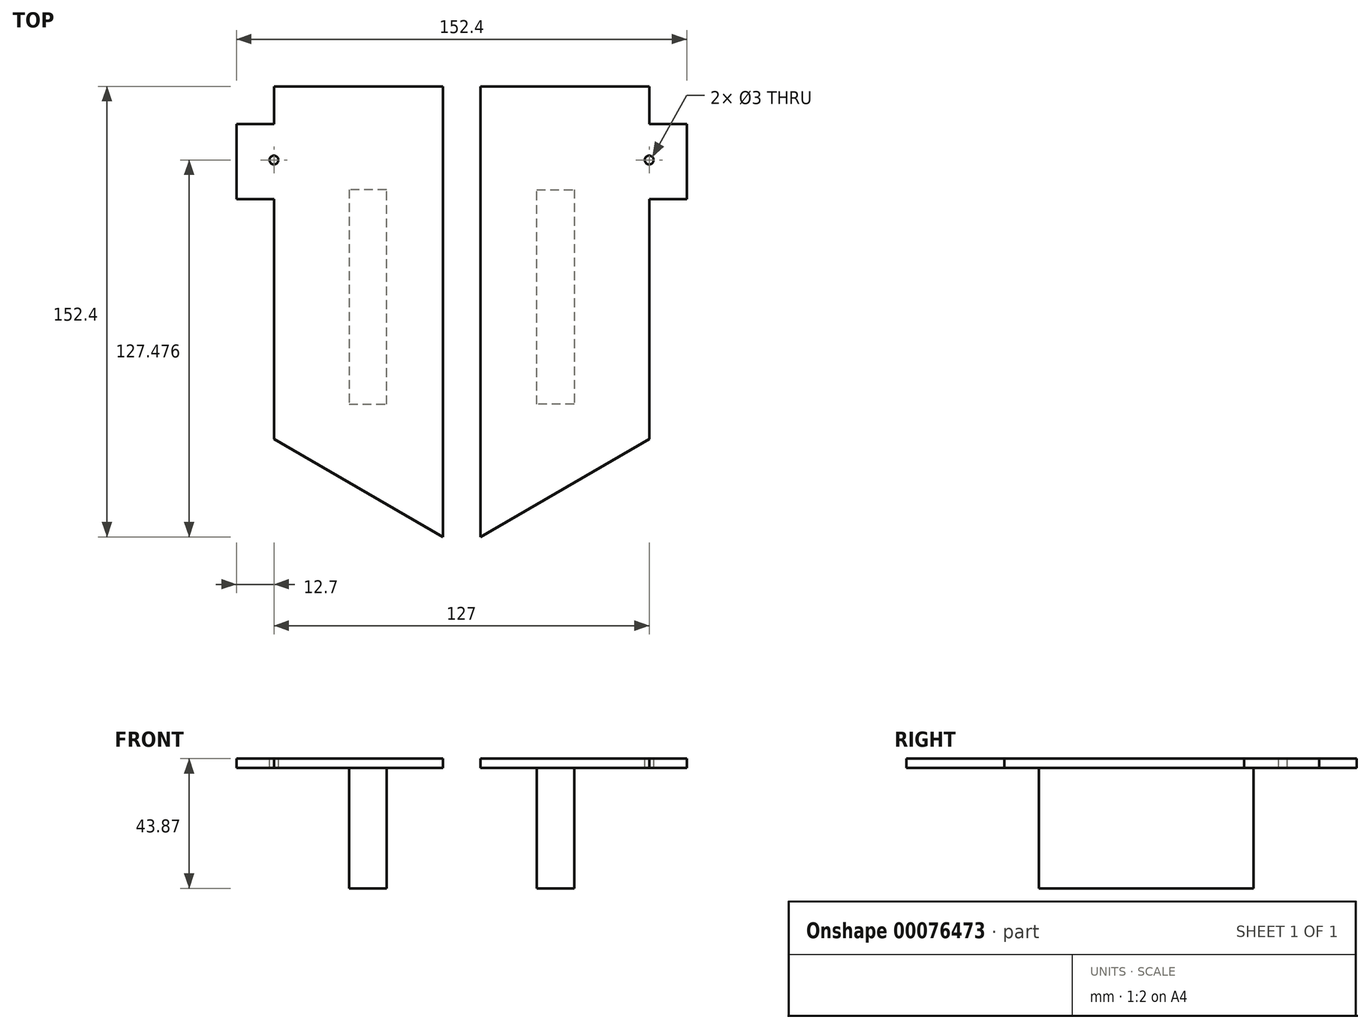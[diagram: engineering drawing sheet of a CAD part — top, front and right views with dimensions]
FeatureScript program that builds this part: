
annotation { "Feature Type Name" : "Feature", "Feature Type Description" : "" }
export const myFeature = defineFeature(function(context is Context, id is Id, definition is map)
    precondition{}
    {
        {
            var Q0;
            Q0=qCreatedBy(makeId("Top.planeOp"),FACE);
            var sketch = newSketch(context, id + "F0", { "sketchPlane" : qUnion([Q0])});
            skLineSegment(sketch, "E0.bottom", {"start": v(-82.55, 213.29) * mm, "end": v(82.55, 213.29) * mm, "construction": true});
            skLineSegment(sketch, "E0.top", {"start": v(-82.55, -66.11) * mm, "end": v(82.55, -66.11) * mm, "construction": true});
            skLineSegment(sketch, "E0.left", {"start": v(-82.55, 213.29) * mm, "end": v(-82.55, -66.11) * mm, "construction": true});
            skLineSegment(sketch, "E0.right", {"start": v(82.55, 213.29) * mm, "end": v(82.55, -66.11) * mm, "construction": true});
            skPoint(sketch, "E1.right.end.orphan", {"position": v(82.55, -193.11) * mm});
            skLineSegment(sketch, "E2", {"start": v(0, 213.29) * mm, "end": v(-25.4, 213.29) * mm});
            skLineSegment(sketch, "E3", {"start": v(0, 213.29) * mm, "end": v(25.4, 213.29) * mm});
            skLineSegment(sketch, "E4", {"start": v(-25.4, 213.29) * mm, "end": v(-25.4, 191.06) * mm});
            skLineSegment(sketch, "E5", {"start": v(25.4, 213.29) * mm, "end": v(25.4, 191.06) * mm});
            skLineSegment(sketch, "E6", {"start": v(-25.4, 191.06) * mm, "end": v(-50.8, 191.06) * mm});
            skLineSegment(sketch, "E7", {"start": v(25.4, 191.06) * mm, "end": v(50.8, 191.06) * mm});
            skLineSegment(sketch, "E8", {"start": v(-50.8, 191.06) * mm, "end": v(-50.8, -66.11) * mm});
            skLineSegment(sketch, "E9", {"start": v(50.8, 191.06) * mm, "end": v(50.8, -66.11) * mm});
            skLineSegment(sketch, "E10", {"start": v(-50.8, -66.11) * mm, "end": v(50.8, -66.11) * mm});
            skLineSegment(sketch, "E11", {"start": v(-25.4, 178.36) * mm, "end": v(25.4, 178.36) * mm});
            skLineSegment(sketch, "E12", {"start": v(-25.4, 178.36) * mm, "end": v(-25.4, 105.77) * mm});
            skLineSegment(sketch, "E13", {"start": v(-25.4, 105.77) * mm, "end": v(25.4, 105.77) * mm});
            skLineSegment(sketch, "E14", {"start": v(25.4, 105.77) * mm, "end": v(25.4, 178.36) * mm});
            skSolve(sketch);
        }
        {
            var Q0;
            Q0=qCreatedBy(makeId("Right.planeOp"),FACE);
            cPlane(context, id + "F1", {"entities" : qUnion([Q0]), "cplaneType" : CPlaneType.OFFSET, "offset" : 76.2 * mm, "width" : 152.4 * mm, "height" : 152.4 * mm});
        }
        {
            var Q0;
            Q0=qCreatedBy(id+"F1.planeOp",FACE);
            var sketch = newSketch(context, id + "F2", { "sketchPlane" : qUnion([Q0])});
            skPoint(sketch, "E15.0", {"position": v(213.29, 0) * mm});
            skPoint(sketch, "E16.0", {"position": v(-66.11, 0) * mm});
            skLineSegment(sketch, "E17", {"start": v(213.29, 3.17) * mm, "end": v(213.29, 0) * mm});
            skLineSegment(sketch, "E18", {"start": v(213.29, 3.17) * mm, "end": v(60.89, 3.17) * mm});
            skLineSegment(sketch, "E19", {"start": v(60.89, 3.17) * mm, "end": v(60.89, 0) * mm});
            skLineSegment(sketch, "E20", {"start": v(60.89, 0) * mm, "end": v(213.29, 0) * mm});
            skSolve(sketch);
        }
        {
            var Q0;
            Q0=makeQuery(id+"F2.imprint","IMPRINT",FACE,{"disambiguationData":[TD([[makeQuery(id+"F2.imprint","IMPRINT",EDGE,{"derivedFrom":sQuery(id+"F2.wireOp",EDGE,"E17")}),-1.0]])]});
            extrude(context, id + "F3", {"entities" : qUnion([Q0]), "oppositeDirection" : true, "depth" : 69.85 * mm});
        }
        {
            var Q0;
            Q0=makeQuery(id+"F3.opExtrude","SWEPT_FACE",FACE,{"disambiguationData":[OSD([sQuery(id+"F2.wireOp",EDGE,"E18")])]});
            var sketch = newSketch(context, id + "F4", { "sketchPlane" : qUnion([Q0])});
            skPoint(sketch, "E21.0", {"position": v(76.2, 213.29) * mm});
            skPoint(sketch, "E22.0", {"position": v(76.2, 60.89) * mm});
            skLineSegment(sketch, "E23", {"start": v(63.5, 213.29) * mm, "end": v(63.5, 60.89) * mm});
            skLineSegment(sketch, "E24", {"start": v(63.5, 200.59) * mm, "end": v(76.2, 200.59) * mm});
            skLineSegment(sketch, "E25", {"start": v(63.5, 175.19) * mm, "end": v(76.2, 175.19) * mm});
            skSolve(sketch);
        }
        {
            var Q0;
            {var subQ4=sQuery(id+"F4.wireOp",EDGE,"E25");Q0=makeQuery(id+"F4.imprint","IMPRINT",FACE,{"disambiguationData":[TD([[makeQuery(id+"F4.imprint","IMPRINT",EDGE,{"derivedFrom":subQ4}),-1.0]])]});}
            var Q1;
            {var subQ4=sQuery(id+"F4.wireOp",EDGE,"E24");Q1=makeQuery(id+"F4.imprint","IMPRINT",FACE,{"disambiguationData":[TD([[makeQuery(id+"F4.imprint","IMPRINT",EDGE,{"derivedFrom":subQ4}),1.0]])]});}
            extrude(context, id + "F5", {"entities" : qUnion([Q0, Q1]), "operationType" : NewBodyOperationType.REMOVE, "oppositeDirection" : true, "depth" : 254 * mm});
        }
        {
            var Q0;
            Q0=makeQuery(id+"F3.opExtrude","SWEPT_FACE",FACE,{"disambiguationData":[OSD([sQuery(id+"F2.wireOp",EDGE,"E19")])]});
            var sketch = newSketch(context, id + "F6", { "sketchPlane" : qUnion([Q0])});
            skPoint(sketch, "E26.0", {"position": v(6.35, 3.17) * mm});
            skPoint(sketch, "E27.0", {"position": v(6.35, 0) * mm});
            skLineSegment(sketch, "E28", {"start": v(6.35, 1.59) * mm, "end": v(6.35, 25.4) * mm});
            skLineSegment(sketch, "E29", {"start": v(6.35, 1.59) * mm, "end": v(6.35, -22.23) * mm});
            skLineSegment(sketch, "E30.bottom", {"start": v(6.35, 25.4) * mm, "end": v(57.15, 25.4) * mm});
            skLineSegment(sketch, "E30.top", {"start": v(6.35, -22.23) * mm, "end": v(57.15, -22.23) * mm});
            skLineSegment(sketch, "E30.left", {"start": v(6.35, 25.4) * mm, "end": v(6.35, -22.23) * mm});
            skLineSegment(sketch, "E30.right", {"start": v(57.15, 25.4) * mm, "end": v(57.15, -22.23) * mm});
            skSolve(sketch);
        }
        {
            var Q0;
            {var subQ0=sQuery(id+"F6.wireOp",EDGE,"E30.bottom");Q0=makeQuery(id+"F6.imprint","IMPRINT",FACE,{"disambiguationData":[TD([[makeQuery(id+"F6.imprint","IMPRINT",EDGE,{"derivedFrom":subQ0}),-1.0]])]});}
            extrude(context, id + "F7", {"entities" : qUnion([Q0]), "operationType" : NewBodyOperationType.REMOVE, "oppositeDirection" : true, "depth" : 254 * mm});
        }
        {
            var Q0;
            Q0=makeQuery(id+"F3.opExtrude","SWEPT_FACE",FACE,{"disambiguationData":[OSD([sQuery(id+"F2.wireOp",EDGE,"E18")])]});
            var sketch = newSketch(context, id + "F8", { "sketchPlane" : qUnion([Q0])});
            skLineSegment(sketch, "E31", {"start": v(6.35, 60.89) * mm, "end": v(63.5, 94.02) * mm});
            skLineSegment(sketch, "E32", {"start": v(63.5, 94.02) * mm, "end": v(63.5, 60.89) * mm});
            skLineSegment(sketch, "E33", {"start": v(63.5, 60.89) * mm, "end": v(6.35, 60.89) * mm});
            skSolve(sketch);
        }
        {
            var Q0;
            Q0=makeQuery(id+"F8.imprint","IMPRINT",FACE,{"disambiguationData":[TD([[makeQuery(id+"F8.imprint","IMPRINT",EDGE,{"derivedFrom":sQuery(id+"F8.wireOp",EDGE,"E31")}),-1.0]])]});
            extrude(context, id + "F9", {"entities" : qUnion([Q0]), "operationType" : NewBodyOperationType.REMOVE, "oppositeDirection" : true, "depth" : 254 * mm});
        }
        {
            var Q0;
            Q0=makeQuery(id+"F3.opExtrude","SWEPT_FACE",FACE,{"disambiguationData":[OSD([sQuery(id+"F2.wireOp",EDGE,"E18")])]});
            var sketch = newSketch(context, id + "F10", { "sketchPlane" : qUnion([Q0])});
            skCircle(sketch, "E34", {"center": v(63.5, 188.37) * mm, "radius": 1.5 * mm});
            skPoint(sketch, "E35.0", {"position": v(50.8, 191.06) * mm});
            skPoint(sketch, "E36.0", {"position": v(82.55, 213.29) * mm});
            skSolve(sketch);
        }
        {
            var Q0;
            Q0=makeQuery(id+"F10.imprint","IMPRINT",FACE,{"disambiguationData":[TD([[makeQuery(id+"F10.imprint","IMPRINT",EDGE,{"derivedFrom":sQuery(id+"F10.wireOp",EDGE,"E34")}),1.0]])]});
            extrude(context, id + "F11", {"entities" : qUnion([Q0]), "operationType" : NewBodyOperationType.REMOVE, "oppositeDirection" : true, "depth" : 254 * mm});
        }
        {
            var Q0;
            Q0=makeQuery(id+"F3.opExtrude","SWEPT_FACE",FACE,{"disambiguationData":[OSD([sQuery(id+"F2.wireOp",EDGE,"E20")])]});
            var sketch = newSketch(context, id + "F12", { "sketchPlane" : qUnion([Q0])});
            skPoint(sketch, "E37.0", {"position": v(25.4, -178.36) * mm});
            skPoint(sketch, "E38.0", {"position": v(25.4, -105.77) * mm});
            skLineSegment(sketch, "E39", {"start": v(25.4, -178.36) * mm, "end": v(63.5, -178.36) * mm});
            skLineSegment(sketch, "E40", {"start": v(63.5, -178.36) * mm, "end": v(63.5, -105.77) * mm});
            skLineSegment(sketch, "E41", {"start": v(63.5, -105.77) * mm, "end": v(25.4, -105.77) * mm});
            skLineSegment(sketch, "E42", {"start": v(25.4, -105.77) * mm, "end": v(25.4, -178.36) * mm});
            skLineSegment(sketch, "E43", {"start": v(38.1, -178.36) * mm, "end": v(38.1, -105.77) * mm});
            skSolve(sketch);
        }
        {
            var Q0;
            Q0=qCreatedBy(makeId("Top.planeOp"),FACE);
            var sketch = newSketch(context, id + "F13", { "sketchPlane" : qUnion([Q0])});
            skPoint(sketch, "E44.0", {"position": v(38.1, 178.36) * mm});
            skLineSegment(sketch, "E45.0", {"start": v(38.1, 178.36) * mm, "end": v(38.1, 105.77) * mm});
            skLineSegment(sketch, "E46.0", {"start": v(25.4, 105.77) * mm, "end": v(25.4, 178.36) * mm});
            skLineSegment(sketch, "E47.0", {"start": v(25.4, 178.36) * mm, "end": v(38.1, 178.36) * mm});
            skPoint(sketch, "E48.orphan", {"position": v(63.5, 178.36) * mm});
            skLineSegment(sketch, "E49.0", {"start": v(38.1, 105.77) * mm, "end": v(25.4, 105.77) * mm});
            skPoint(sketch, "E50.orphan", {"position": v(63.5, 105.77) * mm});
            skSolve(sketch);
        }
        {
            var Q0;
            Q0 = qSketchRegion(id + "F13", true);
            extrude(context, id + "F14", {"entities" : qUnion([Q0]), "operationType" : NewBodyOperationType.ADD, "oppositeDirection" : true, "depth" : 40.7 * mm});
        }
        {
            var Q0;
            Q0=makeQuery(id+"F3.opExtrude","SWEPT_BODY",BODY,{"disambiguationData":[OSD([sQuery(id+"F2.wireOp",EDGE,"E17"),sQuery(id+"F2.wireOp",EDGE,"E18"),sQuery(id+"F2.wireOp",EDGE,"E19"),sQuery(id+"F2.wireOp",EDGE,"E20")])]});
            var Q1;
            Q1=qCreatedBy(makeId("Right.planeOp"),FACE);
            mirror(context, id + "F15", {"entities" : qUnion([Q0]), "mirrorPlane" : qUnion([Q1])});
        }
    });
